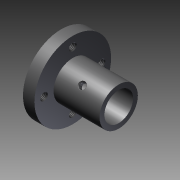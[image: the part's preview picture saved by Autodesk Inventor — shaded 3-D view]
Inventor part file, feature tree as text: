
AUTODESK INVENTOR PART (.ipt)
format: ipt  version: 2011 SP1 (Build 150282100, 282)  size: 152,576 bytes
history: native  units: mm
features: revolve x7, sketch x7, thread x6
ambient origin geometry x8: Origin, YZ Plane, XZ Plane, XY Plane, X Axis, Y Axis, Z Axis, Center Point
bodies: Solid1 (feature_tree)
feature tree (20):
  revolve  "Revolution1"  Angle=360.0deg
  revolve  "Revolution2"  Angle=360.0deg
  thread  "Thread1"  [1 undecoded]
  revolve  "Revolution3"  [1 undecoded]
  thread  "Thread2"  [1 undecoded]
  revolve  "Revolution4"  Angle=360.0deg
  thread  "Thread3"  [1 undecoded]
  revolve  "Revolution5"  [1 undecoded]
  thread  "Thread4"  [1 undecoded]
  revolve  "Revolution6"  [1 undecoded]
  thread  "Thread5"  [1 undecoded]
  revolve  "Revolution7"  [1 undecoded]
  thread  "Thread6"  [1 undecoded]
  sketch  "Sketch_1"  dims[d0=360.0deg d1=360.0deg]
  sketch  "Sketch_3"  dims[d7=360.0deg d8=5.242mm d9=0.0mm d10=360.0deg]
  sketch  "Sketch_2"  dims[d2=2.621mm d3=0.0mm d4=360.0deg d5=2.621mm d6=0.0mm]
  sketch  "Sketch_4"  dims[d11=5.242mm d12=0.0mm d13=360.0deg d14=5.242mm d15=0.0mm]
  sketch  "Sketch_9"  dims[d16=360.0deg d17=5.242mm d18=0.0mm]
  sketch  "Sketch_10"
  sketch  "Sketch_11"
note: 10 required parameter values undecoded (feature->parameter linkage not recoverable at this tier; creation-order binding heuristic only, values carry confidence <= 0.55)